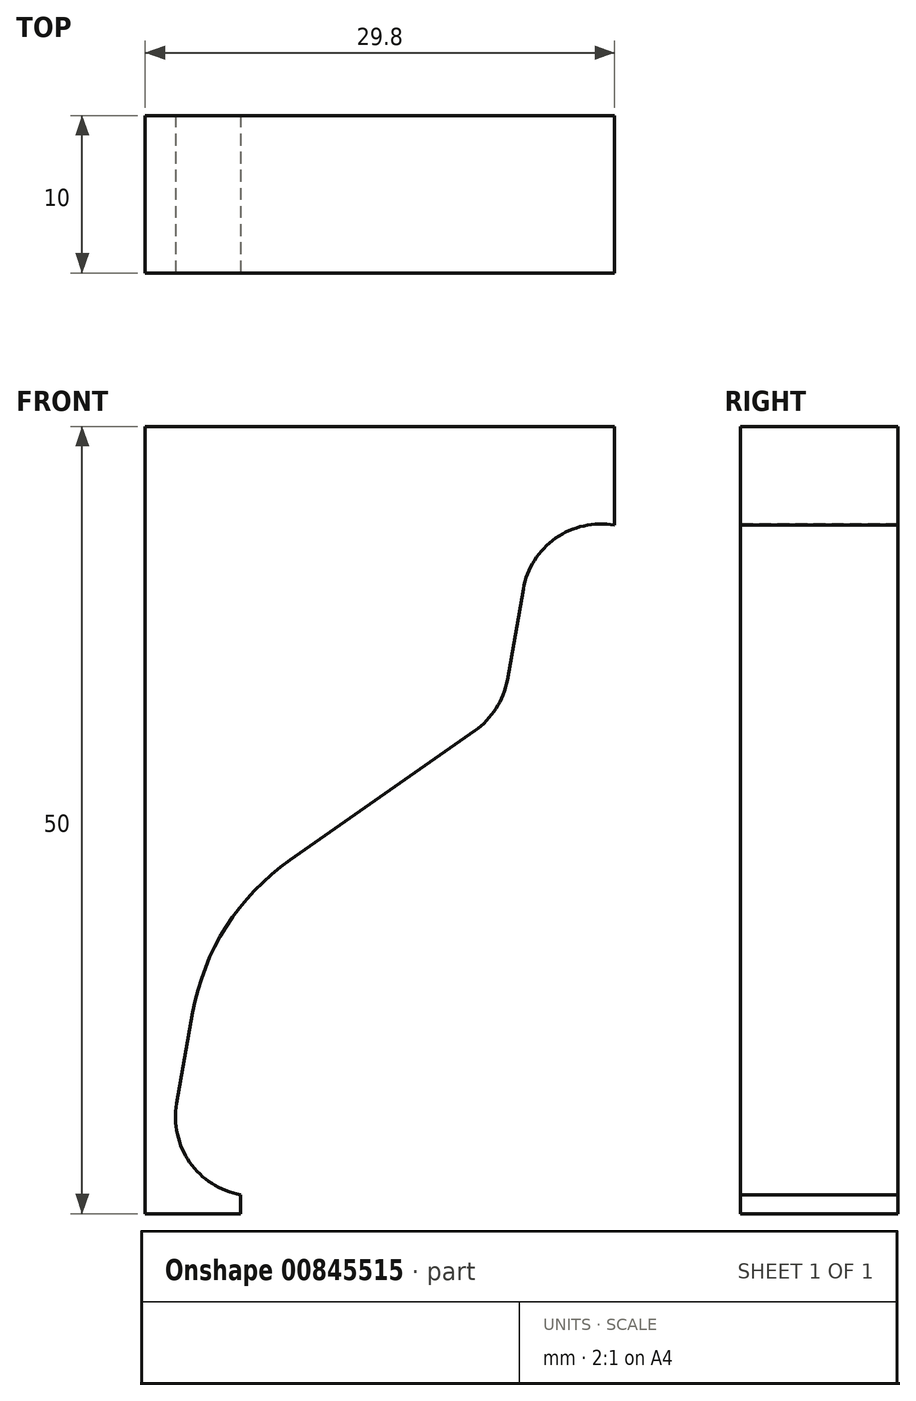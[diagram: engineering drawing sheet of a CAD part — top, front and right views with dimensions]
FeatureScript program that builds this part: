
annotation { "Feature Type Name" : "Feature", "Feature Type Description" : "" }
export const myFeature = defineFeature(function(context is Context, id is Id, definition is map)
    precondition{}
    {
        {
            var Q0;
            Q0=qCreatedBy(makeId("Front.planeOp"),FACE);
            var sketch = newSketch(context, id + "F0", { "sketchPlane" : qUnion([Q0])});
            skLineSegment(sketch, "E0.bottom", {"start": v(0, 0) * mm, "end": v(40, 0) * mm});
            skLineSegment(sketch, "E0.top", {"start": v(0, 50) * mm, "end": v(40, 50) * mm});
            skLineSegment(sketch, "E0.left", {"start": v(0, 0) * mm, "end": v(0, 50) * mm});
            skLineSegment(sketch, "E0.right", {"start": v(40, 0) * mm, "end": v(40, 50) * mm});
            skSolve(sketch);
        }
        {
            var Q0;
            Q0=qSketchRegion(id+"F0",true);
            extrude(context, id + "F1", {"entities" : qUnion([Q0]), "depth" : 10 * mm, "offsetDistance" : 25 * mm});
        }
        {
            var Q0;
            Q0=makeQuery(id+"F1.opExtrude","CAP_FACE",FACE,{"disambiguationData":[OSD([sQuery(id+"F0.wireOp",EDGE,"E0.bottom"),sQuery(id+"F0.wireOp",EDGE,"E0.top"),sQuery(id+"F0.wireOp",EDGE,"E0.left"),sQuery(id+"F0.wireOp",EDGE,"E0.right")])],"isStart":false});
            var sketch = newSketch(context, id + "F2", { "sketchPlane" : qUnion([Q0])});
            skArc(sketch, "E1", {"start": v(2, 7) * mm, "mid": v(2.83, 3.26) * mm, "end": v(6.06, 1.2) * mm});
            skArc(sketch, "E2", {"start": v(29.8, 43.73) * mm, "mid": v(26.06, 42.9) * mm, "end": v(24, 39.68) * mm});
            skLineSegment(sketch, "E3", {"start": v(6.92, 6.13) * mm, "end": v(8.66, 15.98) * mm, "construction": true});
            skLineSegment(sketch, "E4", {"start": v(28.93, 38.8) * mm, "end": v(27.2, 28.96) * mm, "construction": true});
            skLineSegment(sketch, "E5", {"start": v(8.66, 15.98) * mm, "end": v(27.2, 28.96) * mm, "construction": true});
            skLineSegment(sketch, "E6.0", {"start": v(24, 39.68) * mm, "end": v(23, 33.9) * mm});
            skLineSegment(sketch, "E7.0", {"start": v(2, 7) * mm, "end": v(3.02, 12.77) * mm});
            skLineSegment(sketch, "E8.0", {"start": v(9.19, 22.45) * mm, "end": v(20.94, 30.68) * mm});
            skArc(sketch, "E9.filletArc", {"start": v(20.94, 30.68) * mm, "mid": v(22.28, 32.09) * mm, "end": v(23, 33.9) * mm});
            skArc(sketch, "E10.filletArc", {"start": v(9.19, 22.45) * mm, "mid": v(5.14, 18.22) * mm, "end": v(3.02, 12.77) * mm});
            skLineSegment(sketch, "E11.0", {"start": v(6.92, 6.13) * mm, "end": v(22.68, 3.35) * mm, "construction": true});
            skLineSegment(sketch, "E11.1", {"start": v(22.68, 3.35) * mm, "end": v(29.8, 43.73) * mm, "construction": true});
            skLineSegment(sketch, "E11.9", {"start": v(6.92, 6.13) * mm, "end": v(6.92, 6.13) * mm});
            skLineSegment(sketch, "E11.10", {"start": v(6.06, 1.2) * mm, "end": v(8.66, 15.98) * mm, "construction": true});
            skLineSegment(sketch, "E12", {"start": v(29.8, 43.73) * mm, "end": v(29.8, 50) * mm});
            skLineSegment(sketch, "E13", {"start": v(6.06, 1.2) * mm, "end": v(6.06, 0) * mm});
            skLineSegment(sketch, "E14", {"start": v(29.8, 50) * mm, "end": v(40, 50) * mm});
            skLineSegment(sketch, "E15", {"start": v(40, 50) * mm, "end": v(40, 0) * mm});
            skLineSegment(sketch, "E16", {"start": v(40, 0) * mm, "end": v(6.06, 0) * mm});
            skSolve(sketch);
        }
        {
            var Q0;
            Q0 = qSketchRegion(id + "F2", true);
            extrude(context, id + "F3", {"entities" : qUnion([Q0]), "operationType" : NewBodyOperationType.REMOVE, "endBound" : BoundingType.THROUGH_ALL, "oppositeDirection" : true, "depth" : 25 * mm, "offsetDistance" : 25 * mm});
        }
    });
